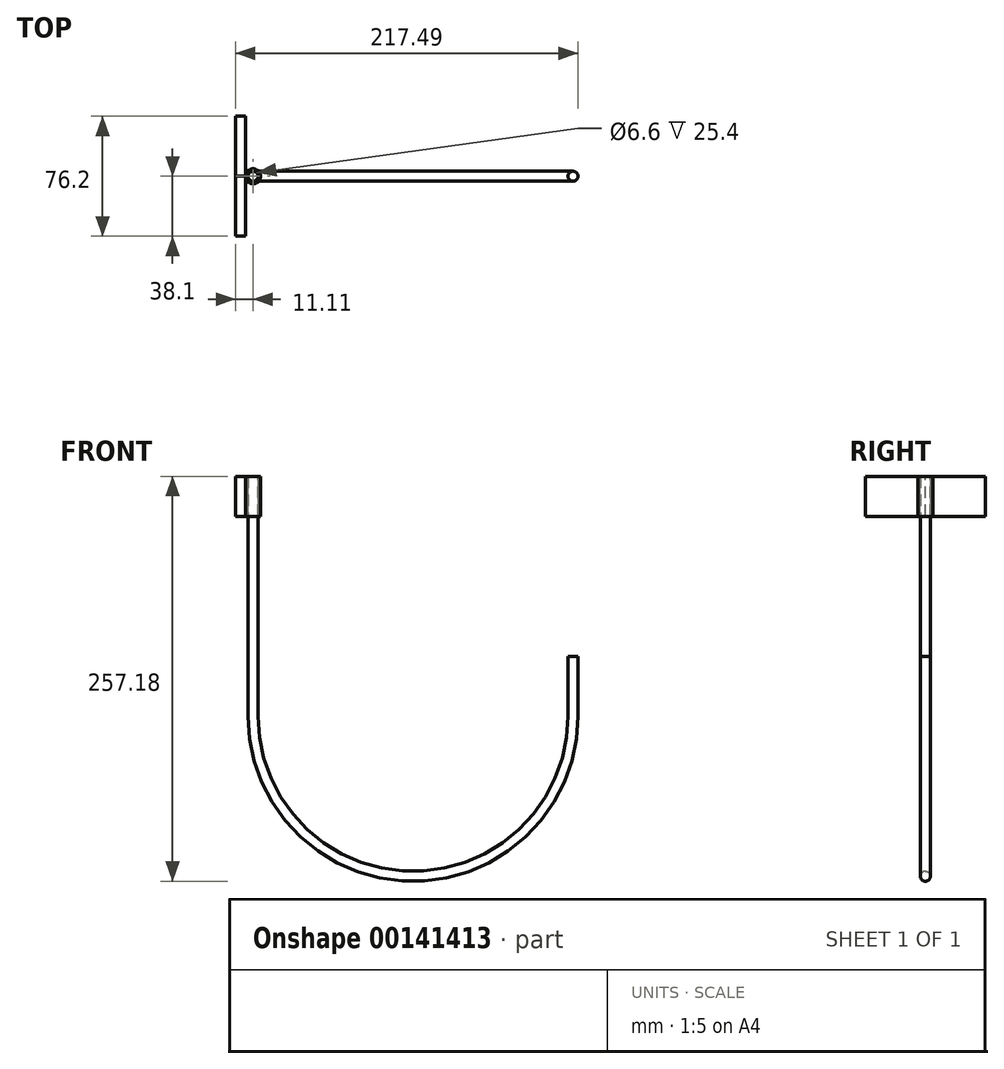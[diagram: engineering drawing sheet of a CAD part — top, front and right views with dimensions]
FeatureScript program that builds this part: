
annotation { "Feature Type Name" : "Feature", "Feature Type Description" : "" }
export const myFeature = defineFeature(function(context is Context, id is Id, definition is map)
    precondition{}
    {
        {
            var Q0;
            Q0=qCreatedBy(makeId("Front.planeOp"),FACE);
            var sketch = newSketch(context, id + "F0", { "sketchPlane" : qUnion([Q0])});
            skLineSegment(sketch, "E0", {"start": v(0, 76.2) * mm, "end": v(0, -76.2) * mm});
            skArc(sketch, "E1", {"start": v(0, -76.2) * mm, "mid": v(101.6, -177.8) * mm, "end": v(203.2, -76.2) * mm});
            skLineSegment(sketch, "E2", {"start": v(203.2, -76.2) * mm, "end": v(203.2, -38.1) * mm});
            skSolve(sketch);
        }
        {
            var Q0;
            Q0=qCreatedBy(makeId("Top.planeOp"),FACE);
            var Q1;
            Q1=sQuery(id+"F0.wireOp",VERTEX,"E0.start");
            cPlane(context, id + "F1", {"entities" : qUnion([Q0, Q1]), "cplaneType" : CPlaneType.PLANE_POINT, "offset" : 25.4 * mm, "width" : 152.4 * mm, "height" : 152.4 * mm});
        }
        {
            var Q0;
            Q0=qCreatedBy(id+"F1.planeOp",FACE);
            var sketch = newSketch(context, id + "F2", { "sketchPlane" : qUnion([Q0])});
            skCircle(sketch, "E3", {"center": v(0, 0) * mm, "radius": 3.18 * mm});
            skSolve(sketch);
        }
        {
            var Q0;
            Q0=makeQuery(id+"F2.imprint","IMPRINT",FACE,{"disambiguationData":[TD([[makeQuery(id+"F2.imprint","IMPRINT",EDGE,{"derivedFrom":sQuery(id+"F2.wireOp",EDGE,"E3")}),1.0]])]});
            var Q1;
            Q1=sQuery(id+"F0.wireOp",EDGE,"E0");
            var Q2;
            Q2=sQuery(id+"F0.wireOp",EDGE,"E1");
            var Q3;
            Q3=sQuery(id+"F0.wireOp",EDGE,"E2");
            sweep(context, id + "F3", {"profiles" : qUnion([Q0]), "path" : qUnion([Q1, Q2, Q3])});
        }
        {
            var Q0;
            Q0=qCreatedBy(id+"F1.planeOp",FACE);
            var sketch = newSketch(context, id + "F4", { "sketchPlane" : qUnion([Q0])});
            skLineSegment(sketch, "E4", {"start": v(-11.11, 38.1) * mm, "end": v(-11.11, -38.1) * mm});
            skLineSegment(sketch, "E5", {"start": v(-11.11, -38.1) * mm, "end": v(-4.76, -38.1) * mm});
            skLineSegment(sketch, "E6", {"start": v(-4.76, -38.1) * mm, "end": v(-4.76, 38.1) * mm});
            skLineSegment(sketch, "E7", {"start": v(-4.76, 38.1) * mm, "end": v(-11.11, 38.1) * mm});
            skCircle(sketch, "E8", {"center": v(0, 0) * mm, "radius": 4.76 * mm});
            skLineSegment(sketch, "E9", {"start": v(-11.11, 0) * mm, "end": v(-4.76, 0) * mm});
            skCircle(sketch, "E10", {"center": v(0, 0) * mm, "radius": 3.3 * mm});
            skSolve(sketch);
        }
        {
            var Q0;
            Q0 = qSketchRegion(id + "F4", true);
            extrude(context, id + "F5", {"entities" : qUnion([Q0]), "operationType" : NewBodyOperationType.ADD, "oppositeDirection" : true, "depth" : 25.4 * mm});
        }
    });
